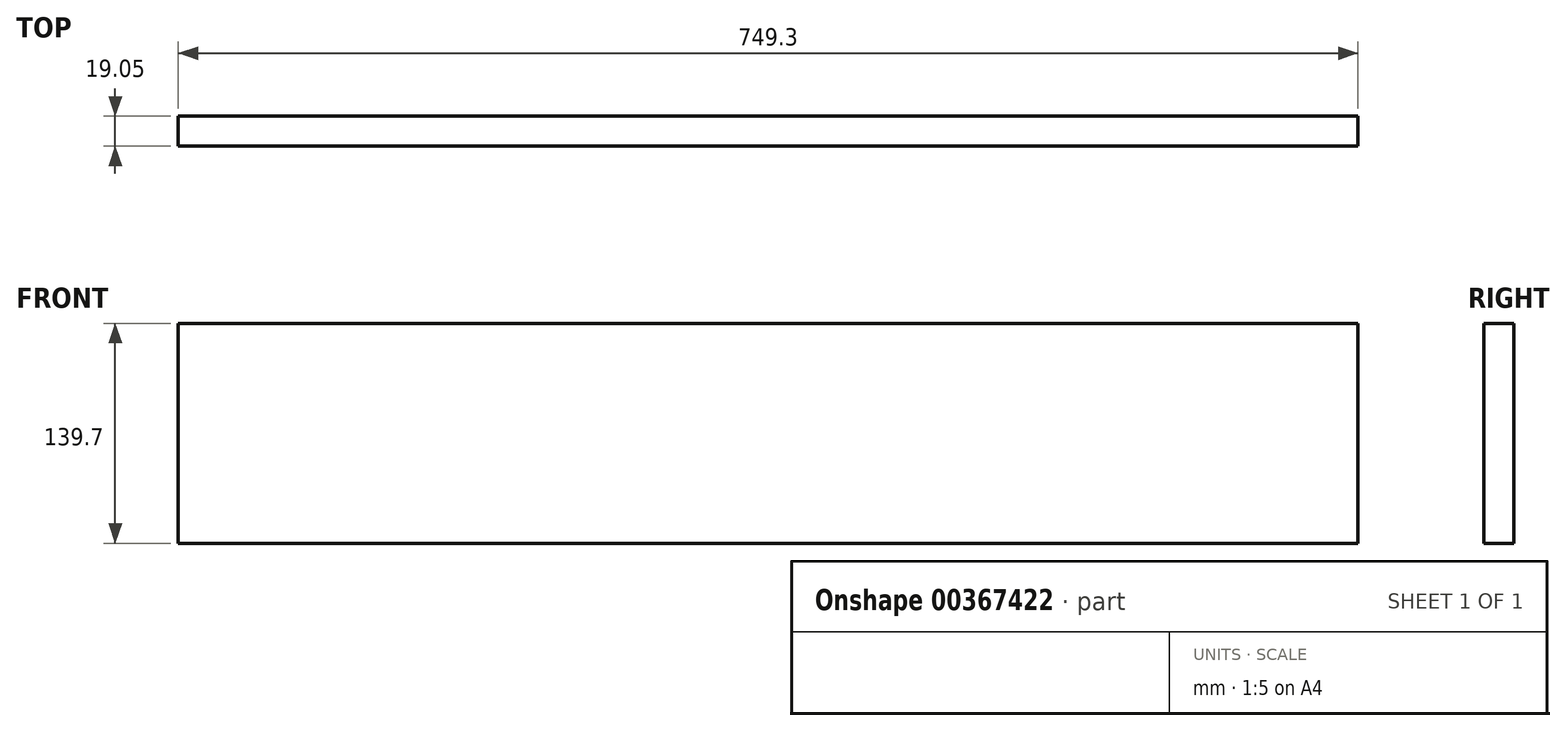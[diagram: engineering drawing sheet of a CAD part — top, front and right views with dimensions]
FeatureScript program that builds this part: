
annotation { "Feature Type Name" : "Feature", "Feature Type Description" : "" }
export const myFeature = defineFeature(function(context is Context, id is Id, definition is map)
    precondition{}
    {
        {
            var Q0;
            Q0=qCreatedBy(makeId("Front.planeOp"),FACE);
            var sketch = newSketch(context, id + "F0", { "sketchPlane" : qUnion([Q0])});
            skLineSegment(sketch, "E0.bottom", {"start": v(374.65, 69.85) * mm, "end": v(-374.65, 69.85) * mm});
            skLineSegment(sketch, "E0.top", {"start": v(374.65, -69.85) * mm, "end": v(-374.65, -69.85) * mm});
            skLineSegment(sketch, "E0.left", {"start": v(374.65, 69.85) * mm, "end": v(374.65, -69.85) * mm});
            skLineSegment(sketch, "E0.right", {"start": v(-374.65, 69.85) * mm, "end": v(-374.65, -69.85) * mm});
            skPoint(sketch, "E0.middle", {"position": v(0, 0) * mm});
            skSolve(sketch);
        }
        {
            var Q0;
            Q0 = qSketchRegion(id + "F0", true);
            extrude(context, id + "F1", {"entities" : qUnion([Q0]), "depth" : 19.05 * mm});
        }
    });
